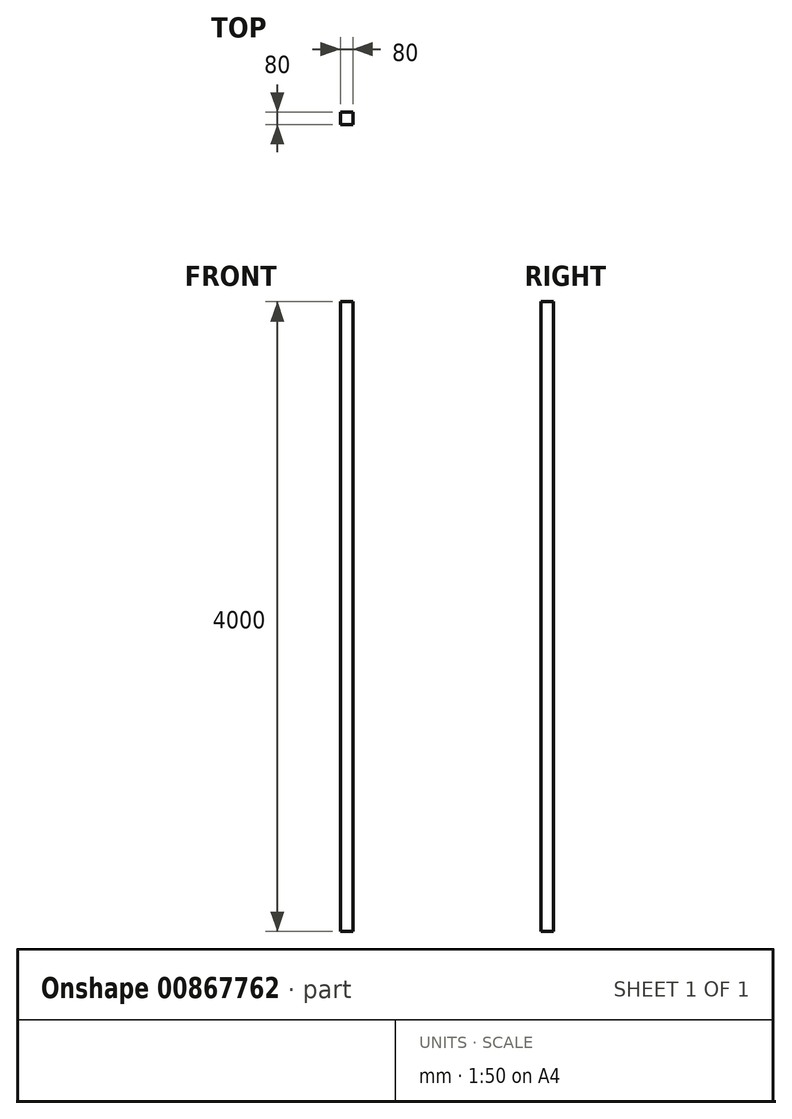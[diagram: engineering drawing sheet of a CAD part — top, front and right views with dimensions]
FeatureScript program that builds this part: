
annotation { "Feature Type Name" : "Feature", "Feature Type Description" : "" }
export const myFeature = defineFeature(function(context is Context, id is Id, definition is map)
    precondition{}
    {
        {
            var Q0;
            Q0=qCreatedBy(makeId("Top.planeOp"),FACE);
            var sketch = newSketch(context, id + "F0", { "sketchPlane" : qUnion([Q0])});
            skLineSegment(sketch, "E0.bottom", {"start": v(40, -40) * mm, "end": v(-40, -40) * mm});
            skLineSegment(sketch, "E0.top", {"start": v(40, 40) * mm, "end": v(-40, 40) * mm});
            skLineSegment(sketch, "E0.left", {"start": v(40, -40) * mm, "end": v(40, 40) * mm});
            skLineSegment(sketch, "E0.right", {"start": v(-40, -40) * mm, "end": v(-40, 40) * mm});
            skPoint(sketch, "E0.middle", {"position": v(0, 0) * mm});
            skSolve(sketch);
        }
        {
            var Q0;
            Q0=makeQuery(id+"F0.imprint","IMPRINT",FACE,{"disambiguationData":[TD([[makeQuery(id+"F0.imprint","IMPRINT",EDGE,{"derivedFrom":sQuery(id+"F0.wireOp",EDGE,"E0.bottom")}),-1.0]])]});
            extrude(context, id + "F1", {"entities" : qUnion([Q0]), "depth" : 4000 * mm, "offsetDistance" : 25 * mm});
        }
    });
